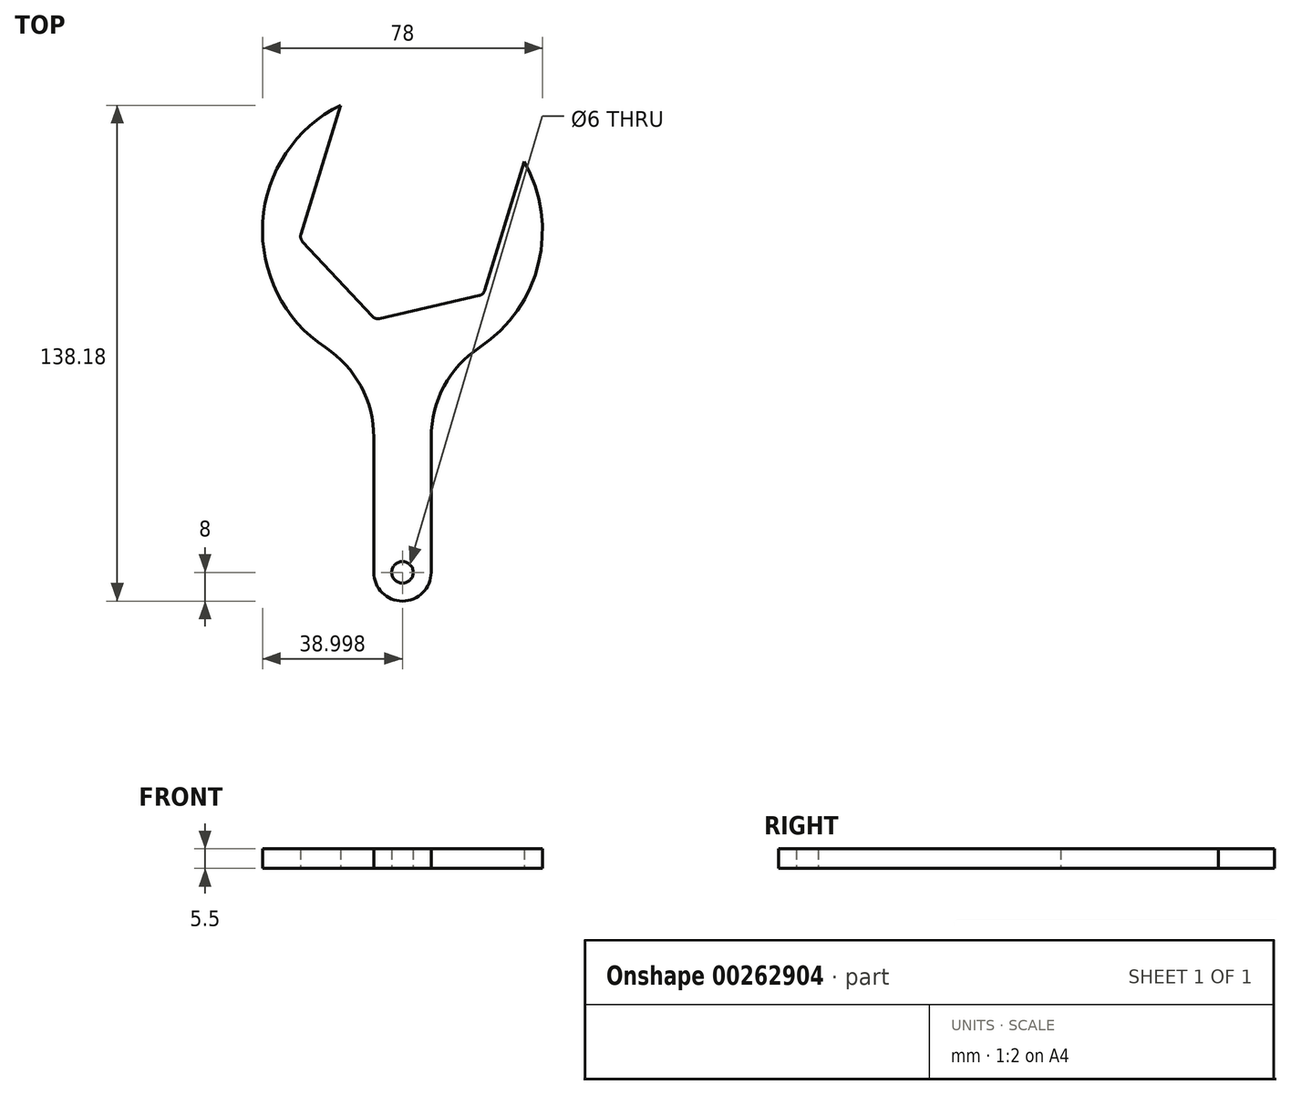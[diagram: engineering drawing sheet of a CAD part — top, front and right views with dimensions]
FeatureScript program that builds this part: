
annotation { "Feature Type Name" : "Feature", "Feature Type Description" : "" }
export const myFeature = defineFeature(function(context is Context, id is Id, definition is map)
    precondition{}
    {
        {
            var Q0;
            Q0=qCreatedBy(makeId("Top.planeOp"),FACE);
            var sketch = newSketch(context, id + "F0", { "sketchPlane" : qUnion([Q0])});
            skCircle(sketch, "E0.cCircle", {"center": v(0, 0) * mm, "radius": 26.75 * mm, "construction": true});
            skLineSegment(sketch, "E0.0", {"start": v(32.42, 14.54) * mm, "end": v(21.4, -21.49) * mm});
            skLineSegment(sketch, "E0.1", {"start": v(19.94, -22.85) * mm, "end": v(-7.9, -29.28) * mm});
            skLineSegment(sketch, "E0.2", {"start": v(-9.82, -28.7) * mm, "end": v(-29.3, -7.8) * mm});
            skLineSegment(sketch, "E0.3", {"start": v(-29.76, -5.84) * mm, "end": v(-18.75, 30.18) * mm});
            skLineSegment(sketch, "E0.4", {"start": v(-21.07, 22.6) * mm, "end": v(9.03, 29.54) * mm, "construction": true});
            skLineSegment(sketch, "E0.5", {"start": v(9.03, 29.54) * mm, "end": v(30.1, 6.95) * mm, "construction": true});
            skPoint(sketch, "E0.0.midPoint", {"position": v(25.58, -7.82) * mm});
            skArc(sketch, "E1", {"start": v(-9.46, -100) * mm, "mid": v(-1.46, -108) * mm, "end": v(6.54, -100) * mm});
            skLineSegment(sketch, "E2.trimOffspring", {"start": v(6.54, -62.37) * mm, "end": v(6.54, -100) * mm});
            skLineSegment(sketch, "E3.trimOffspring", {"start": v(-9.46, -62.37) * mm, "end": v(-9.46, -100) * mm});
            skCircle(sketch, "E4", {"center": v(-1.46, -100) * mm, "radius": 3 * mm});
            skPoint(sketch, "E5.visualSharp", {"position": v(30.1, 6.95) * mm});
            skPoint(sketch, "E6.visualSharp", {"position": v(-21.07, 22.6) * mm});
            skLineSegment(sketch, "E7", {"start": v(-7.82, -25.58) * mm, "end": v(7.82, 25.58) * mm, "construction": true});
            skArc(sketch, "E8", {"start": v(20.02, -37.33) * mm, "mid": v(36.47, -13.85) * mm, "end": v(32.42, 14.54) * mm});
            skArc(sketch, "E9", {"start": v(-9.46, -42.95) * mm, "mid": v(-1.46, -43.78) * mm, "end": v(6.54, -42.95) * mm, "construction": true});
            skLineSegment(sketch, "E10", {"start": v(-1.46, -4.78) * mm, "end": v(-1.46, -100) * mm, "construction": true});
            skLineSegment(sketch, "E11", {"start": v(-18.75, 30.18) * mm, "end": v(-18.75, 30.18) * mm});
            skArc(sketch, "E12", {"start": v(-18.75, 30.18) * mm, "mid": v(-40.39, -2.36) * mm, "end": v(-22.94, -37.33) * mm});
            skArc(sketch, "E13", {"start": v(32.42, 14.54) * mm, "mid": v(9.94, 32.51) * mm, "end": v(-18.75, 30.18) * mm, "construction": true});
            skPoint(sketch, "E14.visualSharp", {"position": v(6.54, -42.95) * mm});
            skArc(sketch, "E14.filletArc", {"start": v(20.02, -37.33) * mm, "mid": v(10.12, -48.16) * mm, "end": v(6.54, -62.37) * mm});
            skPoint(sketch, "E15.visualSharp", {"position": v(-9.46, -42.95) * mm});
            skArc(sketch, "E15.filletArc", {"start": v(-9.46, -62.37) * mm, "mid": v(-13.05, -48.16) * mm, "end": v(-22.94, -37.33) * mm});
            skPoint(sketch, "E16.visualSharp", {"position": v(-30.1, -6.95) * mm});
            skArc(sketch, "E16.filletArc", {"start": v(-29.76, -5.84) * mm, "mid": v(-29.8, -6.88) * mm, "end": v(-29.3, -7.8) * mm});
            skPoint(sketch, "E17.visualSharp", {"position": v(-9.03, -29.54) * mm});
            skArc(sketch, "E17.filletArc", {"start": v(-9.82, -28.7) * mm, "mid": v(-8.94, -29.24) * mm, "end": v(-7.9, -29.28) * mm});
            skPoint(sketch, "E18.visualSharp", {"position": v(21.07, -22.6) * mm});
            skArc(sketch, "E18.filletArc", {"start": v(19.94, -22.85) * mm, "mid": v(20.85, -22.36) * mm, "end": v(21.4, -21.49) * mm});
            skSolve(sketch);
        }
        {
            var Q0;
            Q0=qSketchRegion(id+"F0",true);
            extrude(context, id + "F1", {"entities" : qUnion([Q0]), "depth" : 5.5 * mm});
        }
    });
